annotation { "Feature Type Name" : "Feature", "Feature Type Description" : "" }
export const myFeature = defineFeature(function(context is Context, id is Id, definition is map)
    precondition{}
    {
        {
            var Q0;
            Q0=qCreatedBy(makeId("Top.planeOp"),FACE);
            var sketch = newSketch(context, id + "F0", { "sketchPlane" : qUnion([Q0])});
            skFitSpline(sketch, "E0", {"points": [v(-27.24, -18.7) * mm, v(-24.3, -14.06) * mm, v(-21.97, -12.35) * mm, v(-19.8, -12.5) * mm, v(-16.55, -12.35) * mm, v(-12.06, -8.95) * mm, v(-10.04, -7.55) * mm, v(-10.04, -4.92) * mm, v(-8.65, -3.83) * mm, v(-5.7, -3.68) * mm, v(0, -3.52) * mm, v(0, -2.75) * mm, v(-2.14, -1.5) * mm, v(-4.78, -1.66) * mm, v(-10.97, -1.66) * mm, v(-20.11, -1.66) * mm, v(-31.89, -1.66) * mm, v(-43.2, -1.35) * mm, v(-45.36, -1.5) * mm, v(-46.45, -1.5) * mm, v(-46.76, -1.2) * mm, v(-46.73, -0.7) * mm, v(-46.73, 0.76) * mm, v(-46.04, 1.16) * mm, v(-45.46, 1.45) * mm, v(-44.41, 0.99) * mm, v(-43.08, 0.58) * mm, v(-33.97, 0.76) * mm, v(-25.44, 0.99) * mm, v(-13.77, 1.1) * mm, v(-4.72, 1.22) * mm, v(-2.4, 1.57) * mm, v(-1.3, 3.32) * mm, v(0, 4.27) * mm, v(1.04, 4.53) * mm, v(2.68, 3.92) * mm, v(3.12, 3.58) * mm, v(4.07, 4.44) * mm, v(5.72, 5.66) * mm, v(7.8, 5.83) * mm, v(14.74, 5.83) * mm, v(19.95, 6) * mm, v(22.12, 5.92) * mm, v(23.76, 5.05) * mm, v(25.15, 5.05) * mm, v(26.12, 4.15) * mm, v(32.25, 3.86) * mm, v(33.13, -1.4) * mm, v(32.98, -1.4) * mm, v(25.83, -1.24) * mm, v(25.4, -1.54) * mm, v(25.4, -2.41) * mm, v(24.96, -3.14) * mm, v(29.62, -3.87) * mm, v(36.63, -4.6) * mm, v(42.9, -5.18) * mm, v(47.28, -5.77) * mm, v(52.82, -6.79) * mm, v(54.86, -7.08) * mm, v(55.16, -11.46) * mm, v(53.84, -11.9) * mm, v(53.11, -12.04) * mm, v(55.45, -16.13) * mm, v(54.86, -17.44) * mm, v(52.82, -17.44) * mm, v(52.53, -19.77) * mm, v(51.22, -22.1) * mm, v(48.74, -23.27) * mm, v(45.38, -25.32) * mm, v(41.73, -26.92) * mm, v(41, -27.94) * mm, v(25.83, -28.23) * mm, v(12.4, -28.53) * mm, v(-14.44, -28.67) * mm, v(-18.08, -26.34) * mm, v(-22.02, -23.42) * mm, v(-24.2, -20.21) * mm, v(-24.65, -18.75) * mm, v(-27.24, -18.7) * mm]});
            skLineSegment(sketch, "E1", {"start": v(-46.73, -0.7) * mm, "end": v(54.86, -1.5) * mm, "construction": true});
            skLineSegment(sketch, "E2", {"start": v(11.58, 5.8) * mm, "end": v(12.4, -28.53) * mm, "construction": true});
            skSolve(sketch);
        }
        {
            var Q0;
            Q0 = qSketchRegion(id + "F0", true);
            extrude(context, id + "F1", {"entities" : qUnion([Q0]), "oppositeDirection" : true, "depth" : 6.35 * mm, "offsetDistance" : 25.4 * mm});
        }
        {
            var Q0;
            Q0=makeQuery(id+"F1.opExtrude","CAP_FACE",FACE,{"disambiguationData":[OSD([sQuery(id+"F0.wireOp",EDGE,"E0")])],"isStart":true});
            var sketch = newSketch(context, id + "F2", { "sketchPlane" : qUnion([Q0])});
            skText(sketch, "E3", { "text": "Deputy Dick\n", "fontName": "RobotoSlab-Regular.ttf"});
            const initialGuessF2  = {"E3": [-0.0072, -0.01323, 1, 0, 0.00628]};
            skSetInitialGuess(sketch, initialGuessF2);
            skSolve(sketch);
        }
        {
            var Q0;
            Q0 = qSketchRegion(id + "F2", true);
            extrude(context, id + "F3", {"entities" : qUnion([Q0]), "operationType" : NewBodyOperationType.REMOVE, "oppositeDirection" : true, "depth" : 3.17 * mm, "offsetDistance" : 25.4 * mm});
        }
        {
            var Q0;
            {var subQ0=sQuery(id+"F0.wireOp",EDGE,"E0");Q0=makeQuery(id+"F3.boolean.opBoolean","SPLIT",FACE,{"disambiguationData":[TD([makeQuery(id+"F1.opExtrude","SWEPT_FACE",FACE,{"disambiguationData":[OSD([subQ0])]})])],"derivedFrom":makeQuery(id+"F1.opExtrude","CAP_FACE",FACE,{"disambiguationData":[OSD([subQ0])],"isStart":true})});}
            var sketch = newSketch(context, id + "F4", { "sketchPlane" : qUnion([Q0])});
            skLineSegment(sketch, "E4", {"start": v(10.56, 0) * mm, "end": v(12.84, -1.6) * mm});
            skLineSegment(sketch, "E5", {"start": v(12.84, -1.6) * mm, "end": v(12.02, -4.13) * mm});
            skLineSegment(sketch, "E6", {"start": v(12.17, -4.23) * mm, "end": v(14.26, -2.67) * mm});
            skLineSegment(sketch, "E7", {"start": v(14.26, -2.67) * mm, "end": v(16.45, -4.2) * mm});
            skLineSegment(sketch, "E8", {"start": v(16.56, -4.13) * mm, "end": v(15.75, -1.59) * mm});
            skLineSegment(sketch, "E9", {"start": v(15.75, -1.59) * mm, "end": v(18.03, 0) * mm});
            skLineSegment(sketch, "E10", {"start": v(17.98, 0.18) * mm, "end": v(15.2, 0.18) * mm});
            skLineSegment(sketch, "E11", {"start": v(15.2, 0.18) * mm, "end": v(14.3, 2.87) * mm});
            skLineSegment(sketch, "E12", {"start": v(14.3, 2.87) * mm, "end": v(13.35, 0.22) * mm});
            skLineSegment(sketch, "E13", {"start": v(13.35, 0.22) * mm, "end": v(10.62, 0.22) * mm});
            skArc(sketch, "E14.trimOffspring", {"start": v(16.45, -4.2) * mm, "mid": v(16.5, -4.17) * mm, "end": v(16.56, -4.13) * mm});
            skArc(sketch, "E15.trimOffspring", {"start": v(12.02, -4.13) * mm, "mid": v(12.1, -4.18) * mm, "end": v(12.17, -4.23) * mm});
            skLineSegment(sketch, "E16", {"start": v(10.3, 0.22) * mm, "end": v(10.62, 0.22) * mm});
            skLineSegment(sketch, "E17", {"start": v(10.56, 0) * mm, "end": v(10.3, 0.22) * mm});
            skLineSegment(sketch, "E18", {"start": v(17.98, 0.18) * mm, "end": v(18.18, 0.18) * mm});
            skLineSegment(sketch, "E19", {"start": v(18.18, 0.18) * mm, "end": v(18.03, 0) * mm});
            skSolve(sketch);
        }
        {
            var Q0;
            Q0=makeQuery(id+"F4.imprint","IMPRINT",FACE,{"disambiguationData":[TD([[makeQuery(id+"F4.imprint","IMPRINT",EDGE,{"derivedFrom":sQuery(id+"F4.wireOp",EDGE,"E4")}),1.0]])]});
            extrude(context, id + "F5", {"entities" : qUnion([Q0]), "operationType" : NewBodyOperationType.ADD, "depth" : 3.17 * mm, "offsetDistance" : 25.4 * mm});
        }
    });